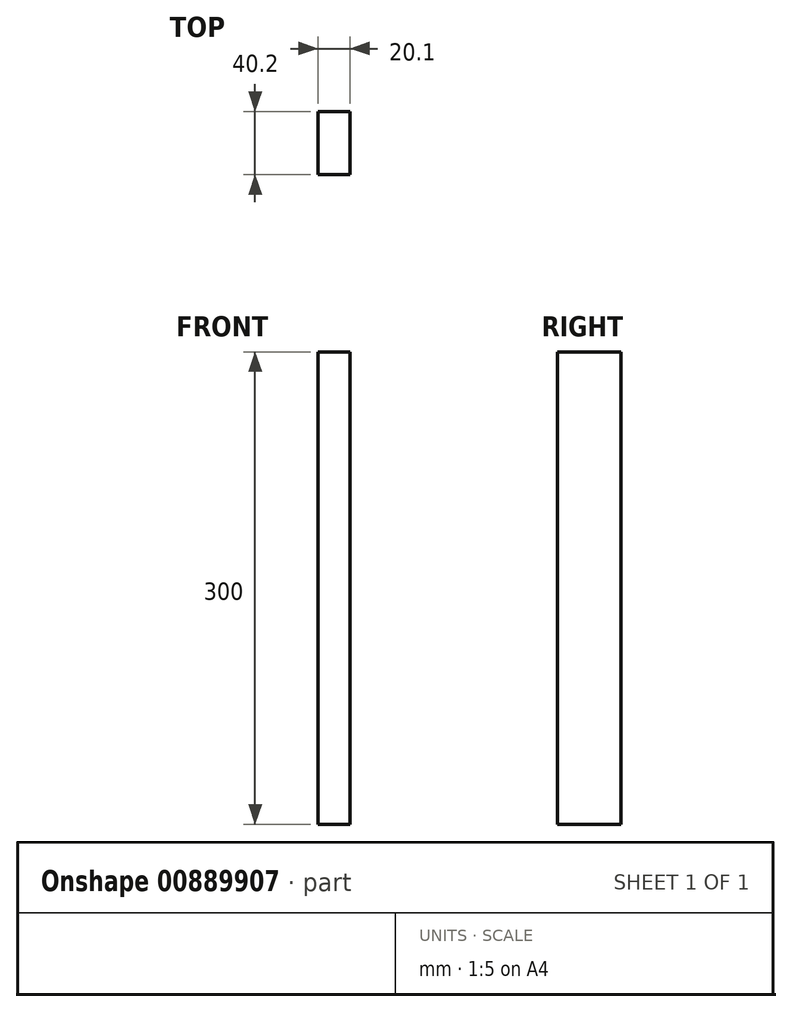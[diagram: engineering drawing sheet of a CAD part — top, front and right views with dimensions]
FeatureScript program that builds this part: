
annotation { "Feature Type Name" : "Feature", "Feature Type Description" : "" }
export const myFeature = defineFeature(function(context is Context, id is Id, definition is map)
    precondition{}
    {
        {
            var Q0;
            Q0=qCreatedBy(makeId("Top.planeOp"),FACE);
            var sketch = newSketch(context, id + "F0", { "sketchPlane" : qUnion([Q0])});
            skLineSegment(sketch, "E0.bottom", {"start": v(0, 0) * mm, "end": v(20.1, 0) * mm});
            skLineSegment(sketch, "E0.top", {"start": v(0, 40.2) * mm, "end": v(20.1, 40.2) * mm});
            skLineSegment(sketch, "E0.left", {"start": v(0, 0) * mm, "end": v(0, 40.2) * mm});
            skLineSegment(sketch, "E0.right", {"start": v(20.1, 0) * mm, "end": v(20.1, 40.2) * mm});
            skSolve(sketch);
        }
        {
            var Q0;
            Q0 = qSketchRegion(id + "F0", true);
            extrude(context, id + "F1", {"entities" : qUnion([Q0]), "depth" : 300 * mm, "offsetDistance" : 25 * mm});
        }
    });
